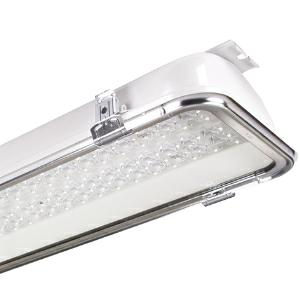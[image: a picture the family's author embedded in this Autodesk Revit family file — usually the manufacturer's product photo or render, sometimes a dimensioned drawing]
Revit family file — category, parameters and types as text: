
# Revit family: 3f_filippi_-_beta_235_76_vt_ampio_3f_filippi_-_52856_-_beta_235_led_761x50_ampio_vt_l1265
name_source: partatom
category: Lighting Fixtures
units: mm (PartAtom-declared; Revit-internal decimal feet)

## family parameters
Cut with Voids When Loaded = No
Host = Face
Light Source = No
Part Type = Normal
Room Calculation Point = No
Round Connector Dimension = Use Diameter
Shared = No

## types (1)
- 3F Filippi - Beta 235 76 VT Ampio (1 x LED, 8367 lm, 54 W, 4000 K)
    Apparent Load = 54 VA
    Approval mark = CE
    CIE Flux Codes = 56 92 99 100 100
    Color Rendering = 80
    Color Temperature = 4000 K
    Control Gear = Electronic ballast
    Default Elevation = 1800 mm
    Description = ILLUMINOTECHNICAL
Luminous efficiency 100% (DLOR 100%, ULOR 0%).
Initial luminous flux of the luminaire 8367 lm.
Wide symmetric distribution.
Installation Interdistance Transv.D = 1.19 x hu - Long.D = 1.18 x hu.
Tabular UGR (CIE 117 - 4H-8H; S=0.25H; 70/50/20): RUG 20.3 - 21.8.
Beam angle: 99° - 105°.
Luminous efficacy 155 lm/W.
Lifetime (L93/B10): 30000 h. (tq+25°C)
Lifetime (L90/B10): 50000 h. (tq+25°C)
Lifetime (L85/B10): 80000 h. (tq+25°C)
Lifetime (L80/B10): 100000 h. (tq+25°C)
Lifetime (L85/B10): 50000 h. (tq+45°C)
Sudden decreased luminous flux after 50000 hours: 0% (C0).
Photobiological safety in compliance with IEC/TR 62778: RG0 risk exempt, (IEC 62471).
In compliance with IEC/EN 62722-2-1 - IEC/EN 62717 standards.

SOURCE
Linear LED module 50W/840.
Energy efficiency class (UE 2019/2020 - UE 2019/2015): C.
CIE 13.3 Colour rendering index: CRI >80 (R9 <50%).
IES TM-30 Fidelity Index: Rf = 84 Rg = 95.
CCT nominal colour temperature 4000 K.
Colour initial tolerance (MacAdam): SDCM 3.

MECHANICAL
Single-piece housing in pressed steel, powder-coated in white epoxy-polyester.
VT transparent glass, non-combustible, single-piece perimeter frame in galvanised steel.
Ecologic anti-aging injected sealing gasket.
Oversized gear-tray reflector unit in highly reflective white painted hot-galvanised steel.
Methacrylate (PMMA) lenses with external flat surface.
Galvanised steel snap-lock clips for diffuser mounting (safety n° 4 per fixture).
Luminaire with limited surface temperature. - D - (EN 60598-2-24)
Dimensions: 1265x235 mm, height 105 mm. Weight 9.14 kg.
IP66 protection degree.
Mechanical strength to impacts IK09 (10 joule).
Glow-wire test resistance 960°C.

ELECTRICAL
Halogen Free electronic wiring 230V-50/60Hz, power factor 0.95, THD <25%, constant output current, class I, 1 driver.
Power of the luminaire 54 W.
ENEC - CE.
Flicker: <4%.
Luminaire compliant with EN 60598-2-22 for power supply from a centralised emergency system CPSS (Central Power Supply System), not incorporated in the luminaire - high risk areas excluded. The default power and flux are 100% in AC and 100% in DC.
Ambient temperature from -20°C to +45°C.
Temperature class T6 max 85°C.
Quick connection via M20 3P connector with 9-13 mm tightening range.
Relative humidity UR: <85%.

INSTALLATION
Ceiling / Suspended / Wall.
All accessories dedicated to this product are available on the Catalog and on our website www.3F-Filippi.com.

APPLICATIONS
Dry, dusty indoor environments, subject to occasional water splashes.
Industrial environments, warehouses, environments where security locks are required on all clips, e.g. prisons (on request).
Environments in which it is necessary a total protection against falling fragments (eg environments with foodstuffs or machines with moving parts or with extreme temperature changes), use luminaires with laminated glass.
Tempered glass is not immune to falling fragments from harmless and caused by shocks or exceptionally derived from the tempering process.

WARNING
Fixture not suitable for cold stores with an ambient temperature <0°C and/or relative humidity >85%.
Luminaire designed for disposal/recycling at end-of-life.
Replaceable (LED only) light source by a professional. Replaceable control gear by a professional.
    Height = 105 mm
    Lamp = 1 x LED
    Lamp Light Flux = 8367 lm
    Lamp Power = 54 W
    Lamp count = 1
    Length = 1265 mm
    Lifetime = 50000 h
    Luminous efficacy = 155 lm/W
    Manufacturer = 3F Filippi
    ModVariant = No
    Model = 3F Filippi - 52856 - Beta 235 LED 761x50 AMPIO VT L1265
    Mounting Place = Ceiling
    Mounting Type = Pendant
    Number of Poles = 1
    OnlyDefault = Yes
    Power Factor = 1
    Product Name = 3F Filippi - Beta 235 76 VT Ampio
    Product group = pendant luminaire
    ProductGroupID = 9
    Protection Class = Protection class I
    Protection Degree = IP 66
    RLX_Detail_Level = 1
    RLX_Emergency_Light_Flux = 0 lm
    RLX_Emergency_Type = 0
    RLX_Emergency_Type_DB = No
    RlxData = <blob elided: 88705 chars, md5=e23a6bb1>
    Socket = socket
    Standby Power = 0 W
    System Light Flux = 8367 lm
    System Power = 54 W
    Type Comments = Product without accessories
    Type Image = 3ffilippi_52856.jpg
    URL = http://relux.com
    VarID = ---
    Voltage = 0 V
    Weight = 0.00 kg
    Width = 235 mm

## geometry (parser evidence)
native form markers: Blend x4, Sweep x12
no freeform markers — native parametric forms only
